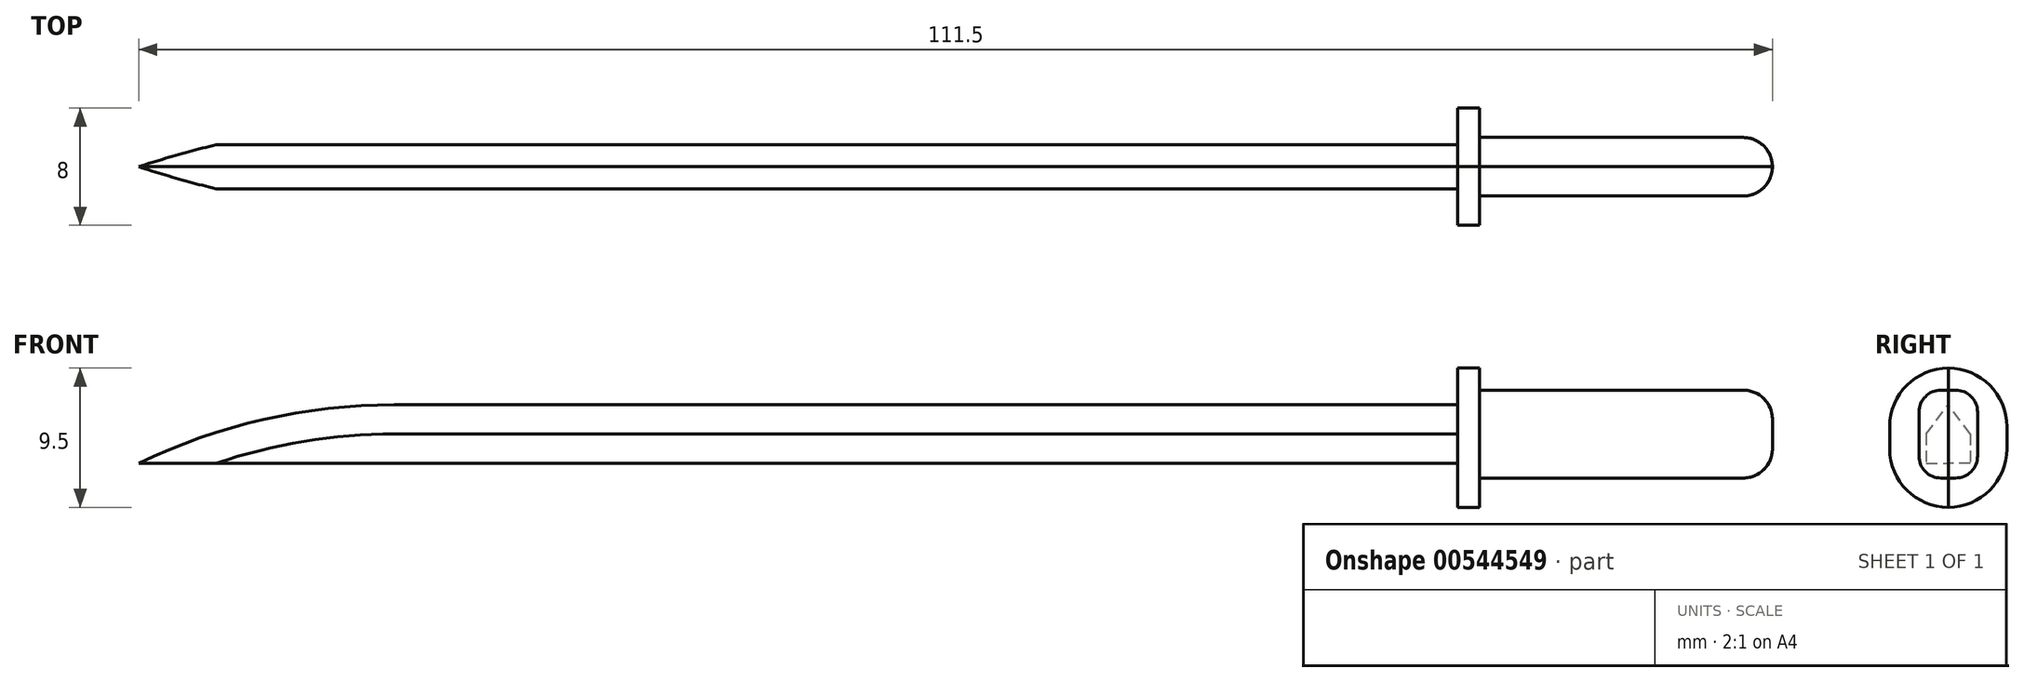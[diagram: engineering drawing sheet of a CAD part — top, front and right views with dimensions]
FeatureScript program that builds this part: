
annotation { "Feature Type Name" : "Feature", "Feature Type Description" : "" }
export const myFeature = defineFeature(function(context is Context, id is Id, definition is map)
    precondition{}
    {
        {
            var Q0;
            Q0=qCreatedBy(makeId("Front.planeOp"),FACE);
            var sketch = newSketch(context, id + "F0", { "sketchPlane" : qUnion([Q0])});
            skLineSegment(sketch, "E0.bottom", {"start": v(0, 0) * mm, "end": v(20, 0) * mm});
            skLineSegment(sketch, "E0.top", {"start": v(0, 6) * mm, "end": v(20, 6) * mm});
            skLineSegment(sketch, "E0.left", {"start": v(0, 0) * mm, "end": v(0, 6) * mm});
            skLineSegment(sketch, "E0.right", {"start": v(20, 0) * mm, "end": v(20, 6) * mm});
            skSolve(sketch);
        }
        {
            var Q0;
            Q0=makeQuery(id+"F0.imprint","IMPRINT",FACE,{"disambiguationData":[TD([[makeQuery(id+"F0.imprint","IMPRINT",EDGE,{"derivedFrom":sQuery(id+"F0.wireOp",EDGE,"E0.bottom")}),1.0]])]});
            extrude(context, id + "F1", {"entities" : qUnion([Q0]), "depth" : 2 * mm, "offsetDistance" : 25 * mm});
        }
        {
            var Q0;
            Q0=makeQuery(id+"F1.opExtrude","CAP_EDGE",EDGE,{"disambiguationData":[OSD([sQuery(id+"F0.wireOp",EDGE,"E0.top")])],"isStart":false});
            var Q1;
            Q1=makeQuery(id+"F1.opExtrude","CAP_EDGE",EDGE,{"disambiguationData":[OSD([sQuery(id+"F0.wireOp",EDGE,"E0.bottom")])],"isStart":false});
            fillet(context, id + "F2", {"entities" : qUnion([Q0, Q1]), "radius" : 1.5 * mm, "tangentPropagation" : true, "allowEdgeOverflow" : false});
        }
        {
            var Q0;
            Q0=makeQuery(id+"F1.opExtrude","CAP_EDGE",EDGE,{"disambiguationData":[OSD([sQuery(id+"F0.wireOp",EDGE,"E0.right")])],"isStart":false});
            fillet(context, id + "F3", {"entities" : qUnion([Q0]), "radius" : 2 * mm, "tangentPropagation" : true, "allowEdgeOverflow" : false});
        }
        {
            var Q0;
            Q0=qCreatedBy(makeId("Front.planeOp"),FACE);
            var sketch = newSketch(context, id + "F4", { "sketchPlane" : qUnion([Q0])});
            skLineSegment(sketch, "E1.bottom", {"start": v(-1.5, 7.5) * mm, "end": v(0, 7.5) * mm});
            skLineSegment(sketch, "E1.top", {"start": v(-1.5, -2) * mm, "end": v(0, -2) * mm});
            skLineSegment(sketch, "E1.left", {"start": v(-1.5, 7.5) * mm, "end": v(-1.5, -2) * mm});
            skLineSegment(sketch, "E1.right", {"start": v(0, 7.5) * mm, "end": v(0, -2) * mm});
            skSolve(sketch);
        }
        {
            var Q0;
            Q0=makeQuery(id+"F4.imprint","IMPRINT",FACE,{"disambiguationData":[TD([[makeQuery(id+"F4.imprint","IMPRINT",EDGE,{"derivedFrom":sQuery(id+"F4.wireOp",EDGE,"E1.bottom")}),-1.0]])]});
            extrude(context, id + "F5", {"entities" : qUnion([Q0]), "depth" : 4 * mm, "offsetDistance" : 25 * mm});
        }
        {
            var Q0;
            Q0=makeQuery(id+"F5.opExtrude","CAP_EDGE",EDGE,{"disambiguationData":[OSD([sQuery(id+"F4.wireOp",EDGE,"E1.top")])],"isStart":false});
            fillet(context, id + "F6", {"entities" : qUnion([Q0]), "radius" : 4 * mm, "tangentPropagation" : true, "allowEdgeOverflow" : false});
        }
        {
            var Q0;
            Q0=makeQuery(id+"F5.opExtrude","CAP_EDGE",EDGE,{"disambiguationData":[OSD([sQuery(id+"F4.wireOp",EDGE,"E1.bottom")])],"isStart":false});
            fillet(context, id + "F7", {"entities" : qUnion([Q0]), "radius" : 4 * mm, "tangentPropagation" : true, "allowEdgeOverflow" : false});
        }
        {
            var Q0;
            Q0=qCreatedBy(makeId("Front.planeOp"),FACE);
            var sketch = newSketch(context, id + "F8", { "sketchPlane" : qUnion([Q0])});
            skLineSegment(sketch, "E2.bottom", {"start": v(-91.5, 5) * mm, "end": v(-1.5, 5) * mm});
            skLineSegment(sketch, "E2.top", {"start": v(-91.5, 1) * mm, "end": v(-1.5, 1) * mm});
            skLineSegment(sketch, "E2.left", {"start": v(-91.5, 5) * mm, "end": v(-91.5, 1) * mm});
            skLineSegment(sketch, "E2.right", {"start": v(-1.5, 5) * mm, "end": v(-1.5, 1) * mm});
            skSolve(sketch);
        }
        {
            var Q0;
            Q0=makeQuery(id+"F8.imprint","IMPRINT",FACE,{"disambiguationData":[TD([[makeQuery(id+"F8.imprint","IMPRINT",EDGE,{"derivedFrom":sQuery(id+"F8.wireOp",EDGE,"E2.bottom")}),-1.0]])]});
            extrude(context, id + "F9", {"entities" : qUnion([Q0]), "depth" : 1.5 * mm, "offsetDistance" : 25 * mm});
        }
        {
            var Q0;
            Q0=makeQuery(id+"F9.opExtrude","SWEPT_EDGE",EDGE,{"disambiguationData":[OSD([sQuery(id+"F8.wireOp",EDGE,"E2.bottom"),sQuery(id+"F8.wireOp",EDGE,"E2.left")])]});
            fillet(context, id + "F10", {"entities" : qUnion([Q0]), "radius" : 40 * mm, "tangentPropagation" : true, "allowEdgeOverflow" : false});
        }
        {
            var Q0;
            Q0=makeQuery(id+"F9.opExtrude","CAP_EDGE",EDGE,{"disambiguationData":[OSD([sQuery(id+"F8.wireOp",EDGE,"E2.bottom")])],"isStart":false});
            chamfer(context, id + "F11", {"entities" : qUnion([Q0]), "chamferType" : ChamferType.TWO_OFFSETS, "width1" : 1.5 * mm, "oppositeDirection" : false, "width2" : 2 * mm, "tangentPropagation" : true});
        }
        {
            var Q0;
            Q0=makeQuery(id+"F1.opExtrude","SWEPT_BODY",BODY,{"disambiguationData":[OSD([sQuery(id+"F0.wireOp",EDGE,"E0.bottom"),sQuery(id+"F0.wireOp",EDGE,"E0.top"),sQuery(id+"F0.wireOp",EDGE,"E0.left"),sQuery(id+"F0.wireOp",EDGE,"E0.right")])]});
            var Q1;
            Q1=makeQuery(id+"F5.opExtrude","SWEPT_BODY",BODY,{"disambiguationData":[OSD([sQuery(id+"F4.wireOp",EDGE,"E1.bottom"),sQuery(id+"F4.wireOp",EDGE,"E1.top"),sQuery(id+"F4.wireOp",EDGE,"E1.left"),sQuery(id+"F4.wireOp",EDGE,"E1.right")])]});
            var Q2;
            Q2=makeQuery(id+"F9.opExtrude","SWEPT_BODY",BODY,{"disambiguationData":[OSD([sQuery(id+"F8.wireOp",EDGE,"E2.bottom"),sQuery(id+"F8.wireOp",EDGE,"E2.top"),sQuery(id+"F8.wireOp",EDGE,"E2.left"),sQuery(id+"F8.wireOp",EDGE,"E2.right")])]});
            var Q3;
            Q3=qCreatedBy(makeId("Front.planeOp"),FACE);
            mirror(context, id + "F12", {"entities" : qUnion([Q0, Q1, Q2]), "mirrorPlane" : qUnion([Q3])});
        }
    });
